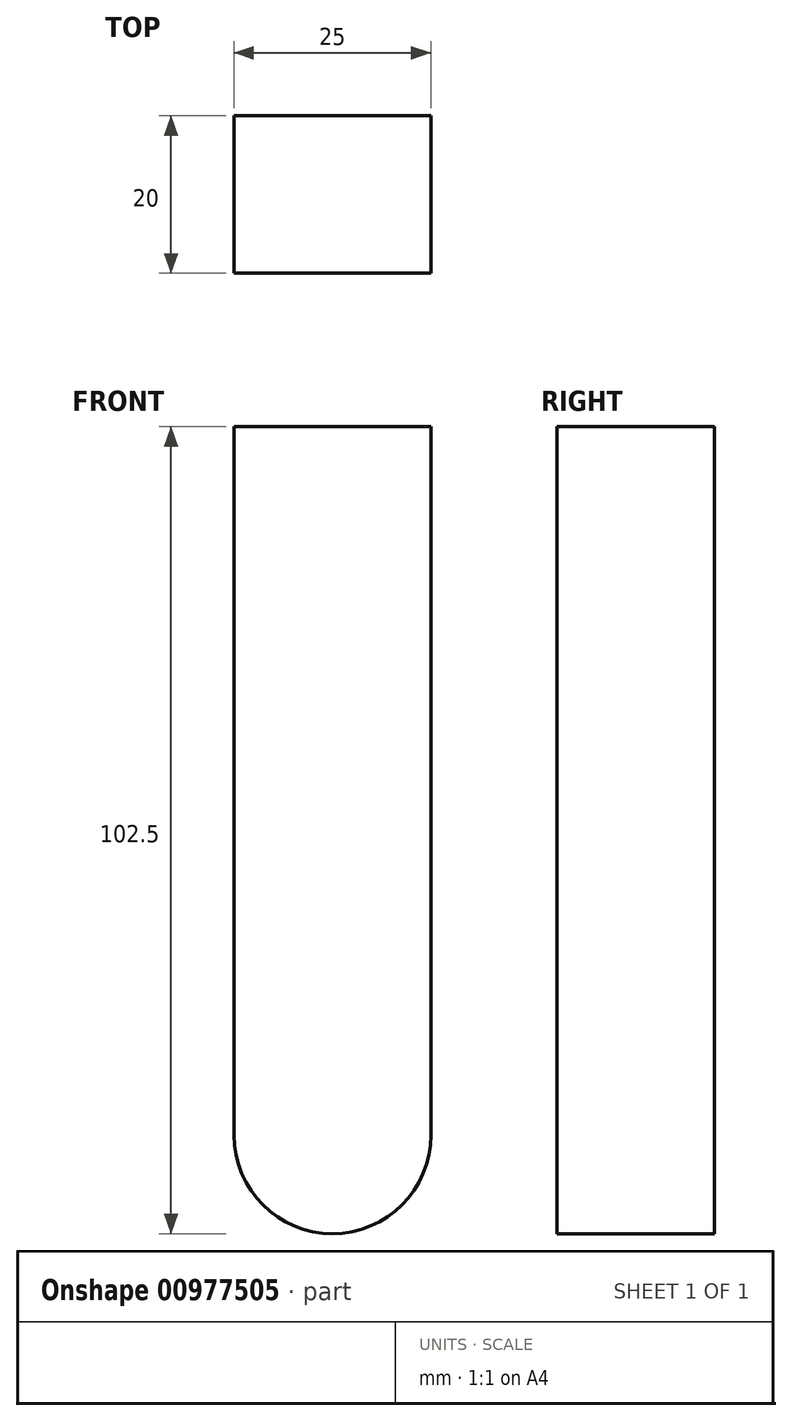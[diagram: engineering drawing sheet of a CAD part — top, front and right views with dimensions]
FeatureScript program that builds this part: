
annotation { "Feature Type Name" : "Feature", "Feature Type Description" : "" }
export const myFeature = defineFeature(function(context is Context, id is Id, definition is map)
    precondition{}
    {
        {
            var Q0;
            Q0=qCreatedBy(makeId("Front.planeOp"),FACE);
            var sketch = newSketch(context, id + "F0", { "sketchPlane" : qUnion([Q0])});
            skLineSegment(sketch, "E0.bottom", {"start": v(-12.5, 45) * mm, "end": v(12.5, 45) * mm});
            skLineSegment(sketch, "E0.left", {"start": v(-12.5, 45) * mm, "end": v(-12.5, -45) * mm});
            skLineSegment(sketch, "E0.right", {"start": v(12.5, 45) * mm, "end": v(12.5, -45) * mm});
            skArc(sketch, "E1", {"start": v(-12.5, -45) * mm, "mid": v(0, -57.5) * mm, "end": v(12.5, -45) * mm});
            skSolve(sketch);
        }
        {
            var Q0;
            Q0 = qSketchRegion(id + "F0", true);
            extrude(context, id + "F1", {"entities" : qUnion([Q0]), "depth" : 20 * mm, "offsetDistance" : 25 * mm});
        }
    });
